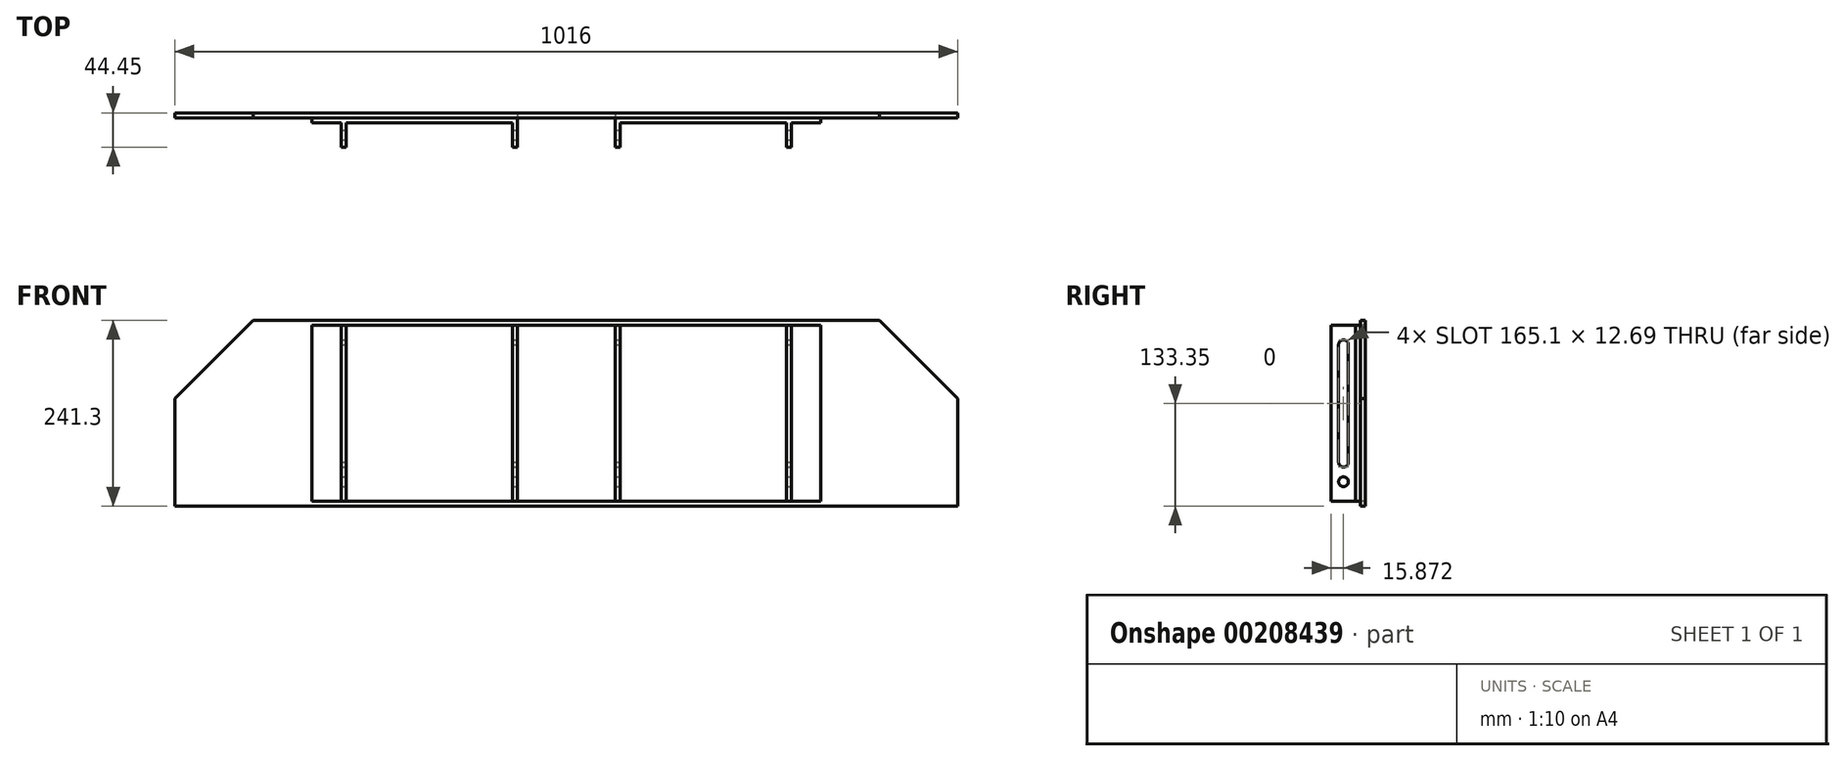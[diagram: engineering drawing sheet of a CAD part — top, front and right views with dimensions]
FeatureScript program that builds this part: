
annotation { "Feature Type Name" : "Feature", "Feature Type Description" : "" }
export const myFeature = defineFeature(function(context is Context, id is Id, definition is map)
    precondition{}
    {
        {
            var Q0;
            Q0=qCreatedBy(makeId("Front.planeOp"),FACE);
            var sketch = newSketch(context, id + "F0", { "sketchPlane" : qUnion([Q0])});
            skLineSegment(sketch, "E0.bottom", {"start": v(-330.2, 114.3) * mm, "end": v(330.2, 114.3) * mm});
            skLineSegment(sketch, "E0.top", {"start": v(-330.2, -114.3) * mm, "end": v(330.2, -114.3) * mm});
            skLineSegment(sketch, "E0.left", {"start": v(-330.2, 114.3) * mm, "end": v(-330.2, -114.3) * mm});
            skLineSegment(sketch, "E0.right", {"start": v(330.2, 114.3) * mm, "end": v(330.2, -114.3) * mm});
            skPoint(sketch, "E0.middle", {"position": v(0, 0) * mm});
            skLineSegment(sketch, "E1.bottom", {"start": v(-330.2, 114.3) * mm, "end": v(-292.1, 114.3) * mm});
            skLineSegment(sketch, "E1.top", {"start": v(-330.2, -114.3) * mm, "end": v(-292.1, -114.3) * mm});
            skLineSegment(sketch, "E2.bottom", {"start": v(330.2, 114.3) * mm, "end": v(292.1, 114.3) * mm});
            skLineSegment(sketch, "E2.top", {"start": v(330.2, -114.3) * mm, "end": v(292.1, -114.3) * mm});
            skLineSegment(sketch, "E3.bottom", {"start": v(-292.1, 114.3) * mm, "end": v(-285.75, 114.3) * mm});
            skLineSegment(sketch, "E3.top", {"start": v(-292.1, -114.3) * mm, "end": v(-285.75, -114.3) * mm});
            skLineSegment(sketch, "E4.bottom", {"start": v(292.1, 114.3) * mm, "end": v(285.75, 114.3) * mm});
            skLineSegment(sketch, "E4.top", {"start": v(292.1, -114.3) * mm, "end": v(285.75, -114.3) * mm});
            skSolve(sketch);
        }
        {
            var Q0;
            Q0=qSketchRegion(id+"F0",true);
            extrude(context, id + "F1", {"entities" : qUnion([Q0]), "depth" : 6.35 * mm});
        }
        {
            var Q0;
            Q0=makeQuery(id+"F1.opExtrude","CAP_FACE",FACE,{"disambiguationData":[OSD([sQuery(id+"F0.wireOp",EDGE,"E0.bottom"),sQuery(id+"F0.wireOp",EDGE,"E0.top"),sQuery(id+"F0.wireOp",EDGE,"E1.bottom"),sQuery(id+"F0.wireOp",EDGE,"E1.top"),sQuery(id+"F0.wireOp",EDGE,"E0.left"),sQuery(id+"F0.wireOp",EDGE,"E2.bottom"),sQuery(id+"F0.wireOp",EDGE,"E2.top"),sQuery(id+"F0.wireOp",EDGE,"E0.right"),sQuery(id+"F0.wireOp",EDGE,"E3.bottom"),sQuery(id+"F0.wireOp",EDGE,"E3.top"),sQuery(id+"F0.wireOp",EDGE,"E4.bottom"),sQuery(id+"F0.wireOp",EDGE,"E4.top")])],"isStart":false});
            var sketch = newSketch(context, id + "F2", { "sketchPlane" : qUnion([Q0])});
            skLineSegment(sketch, "E5.bottom", {"start": v(-330.2, 114.3) * mm, "end": v(-292.1, 114.3) * mm});
            skLineSegment(sketch, "E5.top", {"start": v(-330.2, -114.3) * mm, "end": v(-292.1, -114.3) * mm});
            skLineSegment(sketch, "E5.left", {"start": v(-330.2, 114.3) * mm, "end": v(-330.2, -114.3) * mm});
            skLineSegment(sketch, "E5.right", {"start": v(-292.1, 114.3) * mm, "end": v(-292.1, -114.3) * mm});
            skLineSegment(sketch, "E6.bottom", {"start": v(-292.1, 114.3) * mm, "end": v(-285.75, 114.3) * mm});
            skLineSegment(sketch, "E6.top", {"start": v(-292.1, -114.3) * mm, "end": v(-285.75, -114.3) * mm});
            skLineSegment(sketch, "E6.right", {"start": v(-285.75, 114.3) * mm, "end": v(-285.75, -114.3) * mm});
            skLineSegment(sketch, "E7.bottom", {"start": v(330.2, 114.3) * mm, "end": v(292.1, 114.3) * mm});
            skLineSegment(sketch, "E7.top", {"start": v(330.2, -114.3) * mm, "end": v(292.1, -114.3) * mm});
            skLineSegment(sketch, "E7.left", {"start": v(330.2, 114.3) * mm, "end": v(330.2, -114.3) * mm});
            skLineSegment(sketch, "E7.right", {"start": v(292.1, 114.3) * mm, "end": v(292.1, -114.3) * mm});
            skLineSegment(sketch, "E8.bottom", {"start": v(292.1, 114.3) * mm, "end": v(285.75, 114.3) * mm});
            skLineSegment(sketch, "E8.top", {"start": v(292.1, -114.3) * mm, "end": v(285.75, -114.3) * mm});
            skLineSegment(sketch, "E8.right", {"start": v(285.75, 114.3) * mm, "end": v(285.75, -114.3) * mm});
            skLineSegment(sketch, "E9.bottom", {"start": v(-285.75, 114.3) * mm, "end": v(-69.85, 114.3) * mm});
            skLineSegment(sketch, "E9.top", {"start": v(-285.75, -114.3) * mm, "end": v(-69.85, -114.3) * mm});
            skLineSegment(sketch, "E9.right", {"start": v(-69.85, 114.3) * mm, "end": v(-69.85, -114.3) * mm});
            skLineSegment(sketch, "E10.bottom", {"start": v(-69.85, 114.3) * mm, "end": v(-63.5, 114.3) * mm});
            skLineSegment(sketch, "E10.top", {"start": v(-69.85, -114.3) * mm, "end": v(-63.5, -114.3) * mm});
            skLineSegment(sketch, "E10.right", {"start": v(-63.5, 114.3) * mm, "end": v(-63.5, -114.3) * mm});
            skLineSegment(sketch, "E11.bottom", {"start": v(285.75, 114.3) * mm, "end": v(69.85, 114.3) * mm});
            skLineSegment(sketch, "E11.top", {"start": v(285.75, -114.3) * mm, "end": v(69.85, -114.3) * mm});
            skLineSegment(sketch, "E11.right", {"start": v(69.85, 114.3) * mm, "end": v(69.85, -114.3) * mm});
            skLineSegment(sketch, "E12.bottom", {"start": v(69.85, 114.3) * mm, "end": v(63.5, 114.3) * mm});
            skLineSegment(sketch, "E12.top", {"start": v(69.85, -114.3) * mm, "end": v(63.5, -114.3) * mm});
            skLineSegment(sketch, "E12.right", {"start": v(63.5, 114.3) * mm, "end": v(63.5, -114.3) * mm});
            skSolve(sketch);
        }
        {
            var Q0;
            Q0=makeQuery(id+"F2.imprint","IMPRINT",FACE,{"disambiguationData":[TD([[makeQuery(id+"F2.imprint","IMPRINT",EDGE,{"derivedFrom":sQuery(id+"F2.wireOp",EDGE,"E6.bottom")}),-1.0]])]});
            var Q1;
            Q1=makeQuery(id+"F2.imprint","IMPRINT",FACE,{"disambiguationData":[TD([[makeQuery(id+"F2.imprint","IMPRINT",EDGE,{"derivedFrom":sQuery(id+"F2.wireOp",EDGE,"E8.bottom")}),-1.0]])]});
            var Q2;
            Q2=makeQuery(id+"F2.imprint","IMPRINT",FACE,{"disambiguationData":[TD([[makeQuery(id+"F2.imprint","IMPRINT",EDGE,{"derivedFrom":sQuery(id+"F2.wireOp",EDGE,"E10.bottom")}),-1.0]])]});
            var Q3;
            Q3=makeQuery(id+"F2.imprint","IMPRINT",FACE,{"disambiguationData":[TD([[makeQuery(id+"F2.imprint","IMPRINT",EDGE,{"derivedFrom":sQuery(id+"F2.wireOp",EDGE,"E12.bottom")}),-1.0]])]});
            extrude(context, id + "F3", {"entities" : qUnion([Q0, Q1, Q2, Q3]), "operationType" : NewBodyOperationType.ADD, "depth" : 31.75 * mm});
        }
        {
            var Q0;
            Q0=makeQuery(id+"F3.opExtrude","SWEPT_FACE",FACE,{"disambiguationData":[OSD([sQuery(id+"F2.wireOp",EDGE,"E7.right")])]});
            var sketch = newSketch(context, id + "F4", { "sketchPlane" : qUnion([Q0])});
            skCircle(sketch, "E13", {"center": v(-22.23, -88.9) * mm, "radius": 6.35 * mm});
            skArc(sketch, "E14", {"start": v(-28.58, -63.5) * mm, "mid": v(-22.1, -69.85) * mm, "end": v(-15.88, -63.23) * mm});
            skArc(sketch, "E15", {"start": v(-15.88, 88.63) * mm, "mid": v(-22.1, 95.25) * mm, "end": v(-28.58, 88.9) * mm});
            skLineSegment(sketch, "E16", {"start": v(-28.58, -63.5) * mm, "end": v(-28.58, 88.9) * mm});
            skLineSegment(sketch, "E17", {"start": v(-15.88, -63.23) * mm, "end": v(-15.88, 89.17) * mm});
            skPoint(sketch, "E18.orphan", {"position": v(-22.23, -114.3) * mm});
            skPoint(sketch, "E19.start.orphan", {"position": v(-22.23, 114.3) * mm});
            skSolve(sketch);
        }
        {
            var Q0;
            Q0=qSketchRegion(id+"F4",true);
            extrude(context, id + "F5", {"entities" : qUnion([Q0]), "operationType" : NewBodyOperationType.REMOVE, "oppositeDirection" : true, "depth" : 762 * mm});
        }
        {
            var Q0;
            Q0=makeQuery(id+"F1.opExtrude","CAP_FACE",FACE,{"disambiguationData":[OSD([sQuery(id+"F0.wireOp",EDGE,"E0.bottom"),sQuery(id+"F0.wireOp",EDGE,"E0.top"),sQuery(id+"F0.wireOp",EDGE,"E1.bottom"),sQuery(id+"F0.wireOp",EDGE,"E1.top"),sQuery(id+"F0.wireOp",EDGE,"E0.left"),sQuery(id+"F0.wireOp",EDGE,"E2.bottom"),sQuery(id+"F0.wireOp",EDGE,"E2.top"),sQuery(id+"F0.wireOp",EDGE,"E0.right"),sQuery(id+"F0.wireOp",EDGE,"E3.bottom"),sQuery(id+"F0.wireOp",EDGE,"E3.top"),sQuery(id+"F0.wireOp",EDGE,"E4.bottom"),sQuery(id+"F0.wireOp",EDGE,"E4.top")])],"isStart":true});
            var sketch = newSketch(context, id + "F6", { "sketchPlane" : qUnion([Q0])});
            skLineSegment(sketch, "E20.bottom", {"start": v(-508, 120.65) * mm, "end": v(508, 120.65) * mm});
            skLineSegment(sketch, "E20.top", {"start": v(-508, -120.65) * mm, "end": v(508, -120.65) * mm});
            skLineSegment(sketch, "E20.left", {"start": v(-508, 120.65) * mm, "end": v(-508, -120.65) * mm});
            skLineSegment(sketch, "E20.right", {"start": v(508, 120.65) * mm, "end": v(508, -120.65) * mm});
            skPoint(sketch, "E20.middle", {"position": v(0, 0) * mm});
            skSolve(sketch);
        }
        {
            var Q0;
            Q0=makeQuery(id+"F6.imprint","IMPRINT",FACE,{"disambiguationData":[TD([[makeQuery(id+"F6.imprint","IMPRINT",EDGE,{"derivedFrom":sQuery(id+"F6.wireOp",EDGE,"E20.bottom")}),-1.0]])]});
            var Q1;
            Q1=makeQuery(id+"F6.imprint","IMPRINT",FACE,{"disambiguationData":[TD([[makeQuery(id+"F6.imprint","IMPRINT",EDGE,{"derivedFrom":makeQuery(id+"F1.opExtrude","CAP_EDGE",EDGE,{"disambiguationData":[OSD([sQuery(id+"F0.wireOp",EDGE,"E0.left")])],"isStart":true})}),-1.0]])]});
            extrude(context, id + "F7", {"entities" : qUnion([Q0, Q1]), "depth" : 6.35 * mm});
        }
        {
            var Q0;
            {var subQ0=sQuery(id+"F0.wireOp",EDGE,"E4.bottom");var subQ1=sQuery(id+"F0.wireOp",EDGE,"E3.bottom");var subQ2=sQuery(id+"F0.wireOp",EDGE,"E2.bottom");var subQ3=sQuery(id+"F0.wireOp",EDGE,"E1.bottom");var subQ4=sQuery(id+"F0.wireOp",EDGE,"E0.bottom");var subQ5=sQuery(id+"F0.wireOp",EDGE,"E4.top");var subQ6=sQuery(id+"F0.wireOp",EDGE,"E3.top");var subQ7=sQuery(id+"F0.wireOp",EDGE,"E2.top");var subQ8=sQuery(id+"F0.wireOp",EDGE,"E1.top");var subQ9=sQuery(id+"F0.wireOp",EDGE,"E0.top");Q0=makeQuery(id+"F3.boolean.opBoolean","SPLIT",FACE,{"disambiguationData":[TD([makeQuery(id+"F3.opExtrude","SWEPT_FACE",FACE,{"disambiguationData":[OSD([sQuery(id+"F2.wireOp",EDGE,"E10.right")])]})])],"derivedFrom":makeQuery(id+"F1.opExtrude","CAP_FACE",FACE,{"disambiguationData":[OSD([subQ4,subQ9,subQ3,subQ8,sQuery(id+"F0.wireOp",EDGE,"E0.left"),subQ2,subQ7,sQuery(id+"F0.wireOp",EDGE,"E0.right"),subQ1,subQ6,subQ0,subQ5])],"isStart":false})});}
            extrude(context, id + "F8", {"entities" : qUnion([Q0]), "operationType" : NewBodyOperationType.REMOVE, "oppositeDirection" : true, "depth" : 25.4 * mm});
        }
        {
            var Q0;
            Q0=makeQuery(id+"F8.boolean.opBoolean","SPLIT",BODY,{"disambiguationData":[OD(0.0)],"derivedFrom":makeQuery(id+"F1.opExtrude","SWEPT_BODY",BODY,{"disambiguationData":[OSD([sQuery(id+"F0.wireOp",EDGE,"E0.bottom"),sQuery(id+"F0.wireOp",EDGE,"E0.top"),sQuery(id+"F0.wireOp",EDGE,"E1.bottom"),sQuery(id+"F0.wireOp",EDGE,"E1.top"),sQuery(id+"F0.wireOp",EDGE,"E0.left"),sQuery(id+"F0.wireOp",EDGE,"E2.bottom"),sQuery(id+"F0.wireOp",EDGE,"E2.top"),sQuery(id+"F0.wireOp",EDGE,"E0.right"),sQuery(id+"F0.wireOp",EDGE,"E3.bottom"),sQuery(id+"F0.wireOp",EDGE,"E3.top"),sQuery(id+"F0.wireOp",EDGE,"E4.bottom"),sQuery(id+"F0.wireOp",EDGE,"E4.top")])]})});
            var Q1;
            Q1=makeQuery(id+"F3.opExtrude","SWEPT_FACE",FACE,{"disambiguationData":[OSD([sQuery(id+"F2.wireOp",EDGE,"E5.right")])]});
            transform(context, id + "F9", {"entities" : qUnion([Q0]), "transformType" : TransformType.TRANSLATION_DISTANCE, "transformDirection" : qUnion([Q1]), "distance" : 50.8 * mm, "makeCopy" : false});
        }
        {
            var Q0;
            Q0=makeQuery(id+"F8.boolean.opBoolean","SPLIT",BODY,{"disambiguationData":[OD(1.0)],"derivedFrom":makeQuery(id+"F1.opExtrude","SWEPT_BODY",BODY,{"disambiguationData":[OSD([sQuery(id+"F0.wireOp",EDGE,"E0.bottom"),sQuery(id+"F0.wireOp",EDGE,"E0.top"),sQuery(id+"F0.wireOp",EDGE,"E1.bottom"),sQuery(id+"F0.wireOp",EDGE,"E1.top"),sQuery(id+"F0.wireOp",EDGE,"E0.left"),sQuery(id+"F0.wireOp",EDGE,"E2.bottom"),sQuery(id+"F0.wireOp",EDGE,"E2.top"),sQuery(id+"F0.wireOp",EDGE,"E0.right"),sQuery(id+"F0.wireOp",EDGE,"E3.bottom"),sQuery(id+"F0.wireOp",EDGE,"E3.top"),sQuery(id+"F0.wireOp",EDGE,"E4.bottom"),sQuery(id+"F0.wireOp",EDGE,"E4.top")])]})});
            var Q1;
            Q1=makeQuery(id+"F3.opExtrude","SWEPT_FACE",FACE,{"disambiguationData":[OSD([sQuery(id+"F2.wireOp",EDGE,"E8.right")])]});
            transform(context, id + "F10", {"entities" : qUnion([Q0]), "transformType" : TransformType.TRANSLATION_DISTANCE, "transformDirection" : qUnion([Q1]), "distance" : 50.8 * mm, "oppositeDirection" : true, "makeCopy" : false});
        }
        {
            var Q0;
            Q0=makeQuery(id+"F7.opExtrude","SWEPT_EDGE",EDGE,{"disambiguationData":[OSD([sQuery(id+"F6.wireOp",EDGE,"E20.bottom"),sQuery(id+"F6.wireOp",EDGE,"E20.right")])]});
            var Q1;
            Q1=makeQuery(id+"F7.opExtrude","SWEPT_EDGE",EDGE,{"disambiguationData":[OSD([sQuery(id+"F6.wireOp",EDGE,"E20.bottom"),sQuery(id+"F6.wireOp",EDGE,"E20.left")])]});
            chamfer(context, id + "F11", {"entities" : qUnion([Q0, Q1]), "width" : 101.6 * mm, "tangentPropagation" : true});
        }
    });
